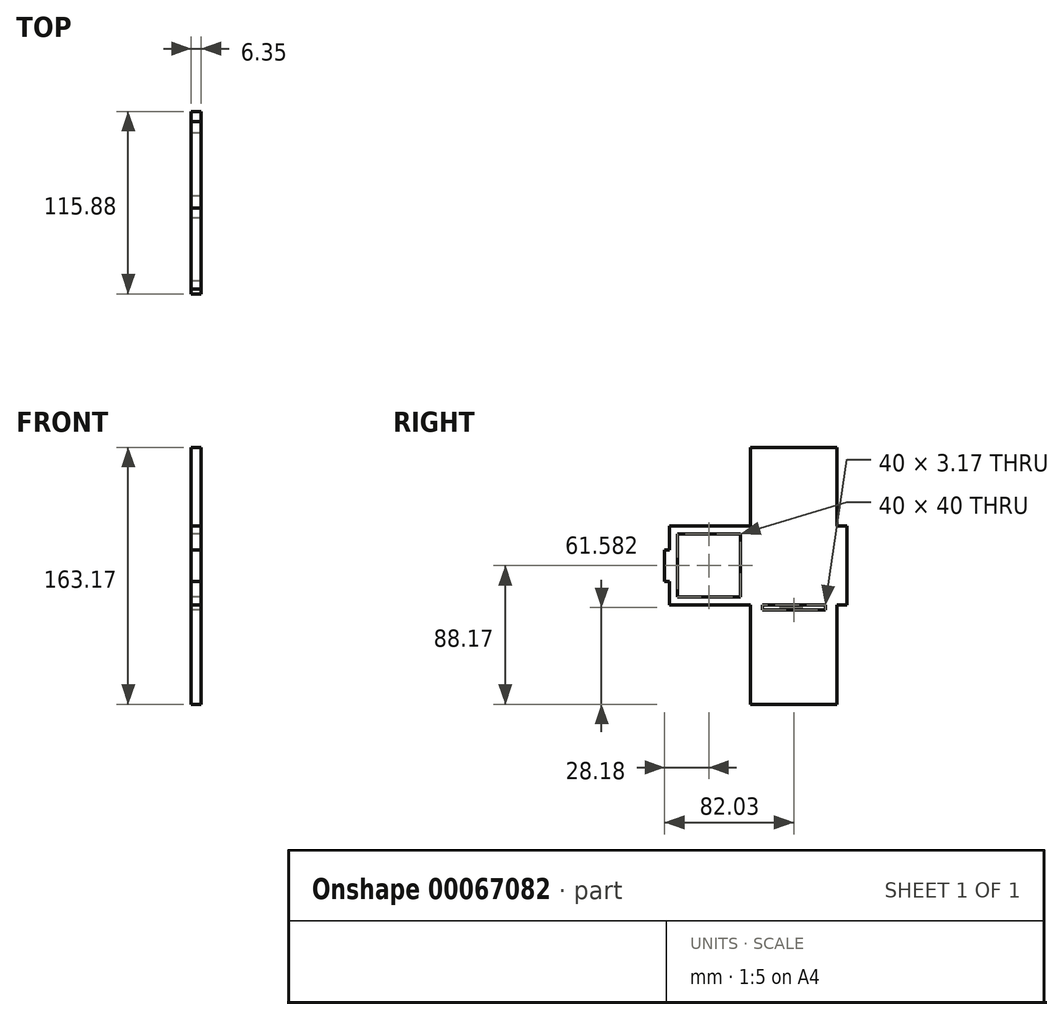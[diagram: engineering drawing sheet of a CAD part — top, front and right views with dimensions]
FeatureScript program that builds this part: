
annotation { "Feature Type Name" : "Feature", "Feature Type Description" : "" }
export const myFeature = defineFeature(function(context is Context, id is Id, definition is map)
    precondition{}
    {
        {
            var Q0;
            Q0=qCreatedBy(makeId("Right.planeOp"),FACE);
            var sketch = newSketch(context, id + "F0", { "sketchPlane" : qUnion([Q0])});
            skLineSegment(sketch, "E0.bottom", {"start": v(-27.5, 0) * mm, "end": v(27.5, 0) * mm});
            skLineSegment(sketch, "E0.top", {"start": v(-27.5, -163.18) * mm, "end": v(27.5, -163.18) * mm});
            skLineSegment(sketch, "E0.left", {"start": v(-27.5, 0) * mm, "end": v(-27.5, -163.18) * mm});
            skLineSegment(sketch, "E0.right", {"start": v(27.5, 0) * mm, "end": v(27.5, -163.18) * mm});
            skLineSegment(sketch, "E1.bottom", {"start": v(-20, -100) * mm, "end": v(20, -100) * mm});
            skLineSegment(sketch, "E1.top", {"start": v(-20, -103.18) * mm, "end": v(20, -103.18) * mm});
            skLineSegment(sketch, "E1.left", {"start": v(-20, -100) * mm, "end": v(-20, -103.18) * mm});
            skLineSegment(sketch, "E1.right", {"start": v(20, -100) * mm, "end": v(20, -103.17) * mm});
            skLineSegment(sketch, "E2", {"start": v(-20, -103.18) * mm, "end": v(-27.5, -103.18) * mm, "construction": true});
            skLineSegment(sketch, "E3", {"start": v(20, -103.18) * mm, "end": v(27.5, -103.18) * mm, "construction": true});
            skLineSegment(sketch, "E4.bottom", {"start": v(27.5, -50) * mm, "end": v(33.85, -50) * mm});
            skLineSegment(sketch, "E4.top", {"start": v(27.5, -100) * mm, "end": v(33.85, -100) * mm});
            skLineSegment(sketch, "E4.left", {"start": v(27.5, -50) * mm, "end": v(27.5, -100) * mm});
            skLineSegment(sketch, "E4.right", {"start": v(33.85, -50) * mm, "end": v(33.85, -100) * mm});
            skLineSegment(sketch, "E5.bottom", {"start": v(-27.5, -50) * mm, "end": v(-78.85, -50) * mm});
            skLineSegment(sketch, "E5.top", {"start": v(-27.5, -100) * mm, "end": v(-78.85, -100) * mm});
            skLineSegment(sketch, "E5.left", {"start": v(-27.5, -50) * mm, "end": v(-27.5, -100) * mm});
            skLineSegment(sketch, "E5.right", {"start": v(-78.85, -50) * mm, "end": v(-78.85, -100) * mm});
            skLineSegment(sketch, "E6.bottom", {"start": v(-73.85, -55) * mm, "end": v(-33.85, -55) * mm});
            skLineSegment(sketch, "E6.top", {"start": v(-73.85, -95) * mm, "end": v(-33.85, -95) * mm});
            skLineSegment(sketch, "E6.left", {"start": v(-73.85, -55) * mm, "end": v(-73.85, -95) * mm});
            skLineSegment(sketch, "E6.right", {"start": v(-33.85, -55) * mm, "end": v(-33.85, -95) * mm});
            skLineSegment(sketch, "E7", {"start": v(-53.18, -55) * mm, "end": v(-53.18, -50) * mm, "construction": true});
            skPoint(sketch, "E7.startSnap0", {"position": v(-53.17, -50) * mm});
            skLineSegment(sketch, "E8", {"start": v(-53.18, -95) * mm, "end": v(-53.18, -100) * mm, "construction": true});
            skLineSegment(sketch, "E9.bottom", {"start": v(-78.85, -65) * mm, "end": v(-82.02, -65) * mm});
            skLineSegment(sketch, "E9.top", {"start": v(-78.85, -85) * mm, "end": v(-82.02, -85) * mm});
            skLineSegment(sketch, "E9.left", {"start": v(-78.85, -65) * mm, "end": v(-78.85, -85) * mm});
            skLineSegment(sketch, "E9.right", {"start": v(-82.02, -65) * mm, "end": v(-82.02, -85) * mm});
            skLineSegment(sketch, "E10", {"start": v(-82.02, -65) * mm, "end": v(-78.85, -50) * mm, "construction": true});
            skLineSegment(sketch, "E11", {"start": v(-82.02, -85) * mm, "end": v(-78.85, -100) * mm, "construction": true});
            skSolve(sketch);
        }
        {
            var Q0;
            {var subQ0=sQuery(id+"F0.wireOp",EDGE,"E0.bottom");Q0=makeQuery(id+"F0.imprint","IMPRINT",FACE,{"disambiguationData":[TD([[makeQuery(id+"F0.imprint","IMPRINT",EDGE,{"derivedFrom":subQ0}),-1.0]])]});}
            var Q1;
            Q1=makeQuery(id+"F0.imprint","IMPRINT",FACE,{"disambiguationData":[TD([[makeQuery(id+"F0.imprint","IMPRINT",EDGE,{"derivedFrom":sQuery(id+"F0.wireOp",EDGE,"E4.bottom")}),-1.0]])]});
            var Q2;
            {var subQ1=sQuery(id+"F0.wireOp",EDGE,"E5.bottom");Q2=makeQuery(id+"F0.imprint","IMPRINT",FACE,{"disambiguationData":[TD([[makeQuery(id+"F0.imprint","IMPRINT",EDGE,{"derivedFrom":subQ1}),1.0]])]});}
            var Q3;
            Q3=makeQuery(id+"F0.imprint","IMPRINT",FACE,{"disambiguationData":[TD([[makeQuery(id+"F0.imprint","IMPRINT",EDGE,{"derivedFrom":sQuery(id+"F0.wireOp",EDGE,"E9.bottom")}),1.0]])]});
            extrude(context, id + "F1", {"entities" : qUnion([Q0, Q1, Q2, Q3]), "depth" : 6.35 * mm});
        }
    });
